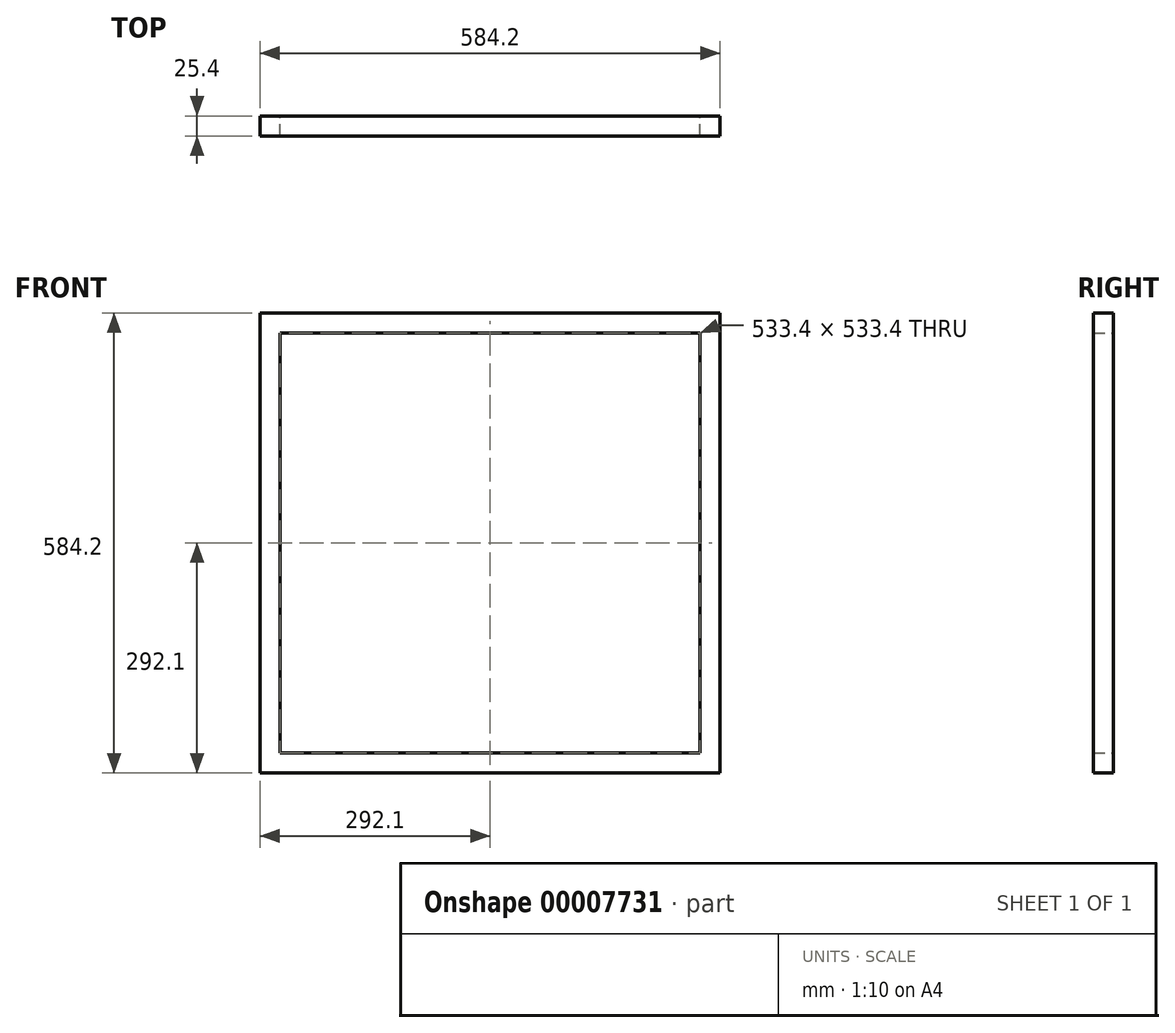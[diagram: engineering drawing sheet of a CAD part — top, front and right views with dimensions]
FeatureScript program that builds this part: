
annotation { "Feature Type Name" : "Feature", "Feature Type Description" : "" }
export const myFeature = defineFeature(function(context is Context, id is Id, definition is map)
    precondition{}
    {
        {
            var Q0;
            Q0=qCreatedBy(makeId("Front.planeOp"),FACE);
            var sketch = newSketch(context, id + "F0", { "sketchPlane" : qUnion([Q0])});
            skLineSegment(sketch, "E0.bottom", {"start": v(0, 0) * mm, "end": v(584.2, 0) * mm});
            skLineSegment(sketch, "E0.top", {"start": v(0, 584.2) * mm, "end": v(584.2, 584.2) * mm});
            skLineSegment(sketch, "E0.left", {"start": v(0, 0) * mm, "end": v(0, 584.2) * mm});
            skLineSegment(sketch, "E0.right", {"start": v(584.2, 0) * mm, "end": v(584.2, 584.2) * mm});
            skLineSegment(sketch, "E1.bottom", {"start": v(25.4, 25.4) * mm, "end": v(558.8, 25.4) * mm});
            skLineSegment(sketch, "E1.top", {"start": v(25.4, 558.8) * mm, "end": v(558.8, 558.8) * mm});
            skLineSegment(sketch, "E1.left", {"start": v(25.4, 25.4) * mm, "end": v(25.4, 558.8) * mm});
            skLineSegment(sketch, "E1.right", {"start": v(558.8, 25.4) * mm, "end": v(558.8, 558.8) * mm});
            skSolve(sketch);
        }
        {
            var Q0;
            Q0=makeQuery(id+"F0.imprint","IMPRINT",FACE,{"disambiguationData":[TD([[makeQuery(id+"F0.imprint","IMPRINT",EDGE,{"derivedFrom":sQuery(id+"F0.wireOp",EDGE,"E0.bottom")}),1.0]])]});
            extrude(context, id + "F1", {"entities" : qUnion([Q0]), "depth" : 25.4 * mm});
        }
    });
